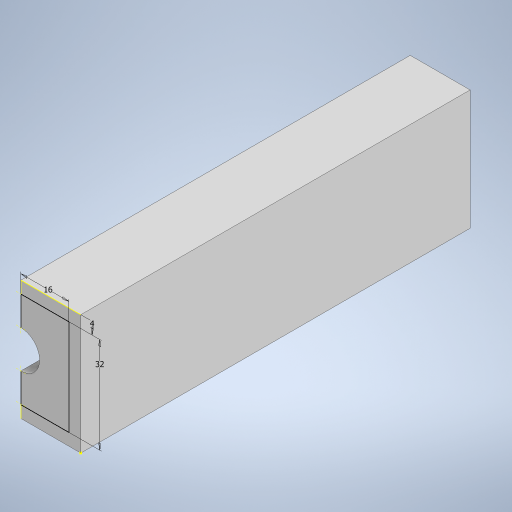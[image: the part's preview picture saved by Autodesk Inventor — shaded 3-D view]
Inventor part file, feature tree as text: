
AUTODESK INVENTOR PART (.ipt)
format: ipt  version: 2023 (Build 270158000, 158)  size: 244,224 bytes
history: native  units: in
note: dims shown in document units (in); Inventor stores cm internally (conversion verified against a paired STEP export)
features: sketch x7, extrude x3, other x1
ambient origin geometry x8: Origin, YZ Plane, XZ Plane, XY Plane, X Axis, Y Axis, Z Axis, Center Point
bodies: Body1 (feature_tree), Body2 (feature_tree), Body3 (feature_tree), Body4 (feature_tree), Body5 (feature_tree), Body6 (feature_tree)
feature tree (11):
  other  "솔리드1"
  extrude  "돌출1"  Depth=1.5748in
  sketch  "스케치2"
  sketch  "스케치3"
  sketch  "스케치4"
  sketch  "스케치5"
  extrude  "돌출2"  Depth=0.7874in
  extrude  "돌출3"  Depth=0.7874in
  sketch  "스케치1"
  sketch  "스케치6"
  sketch  "스케치7"
